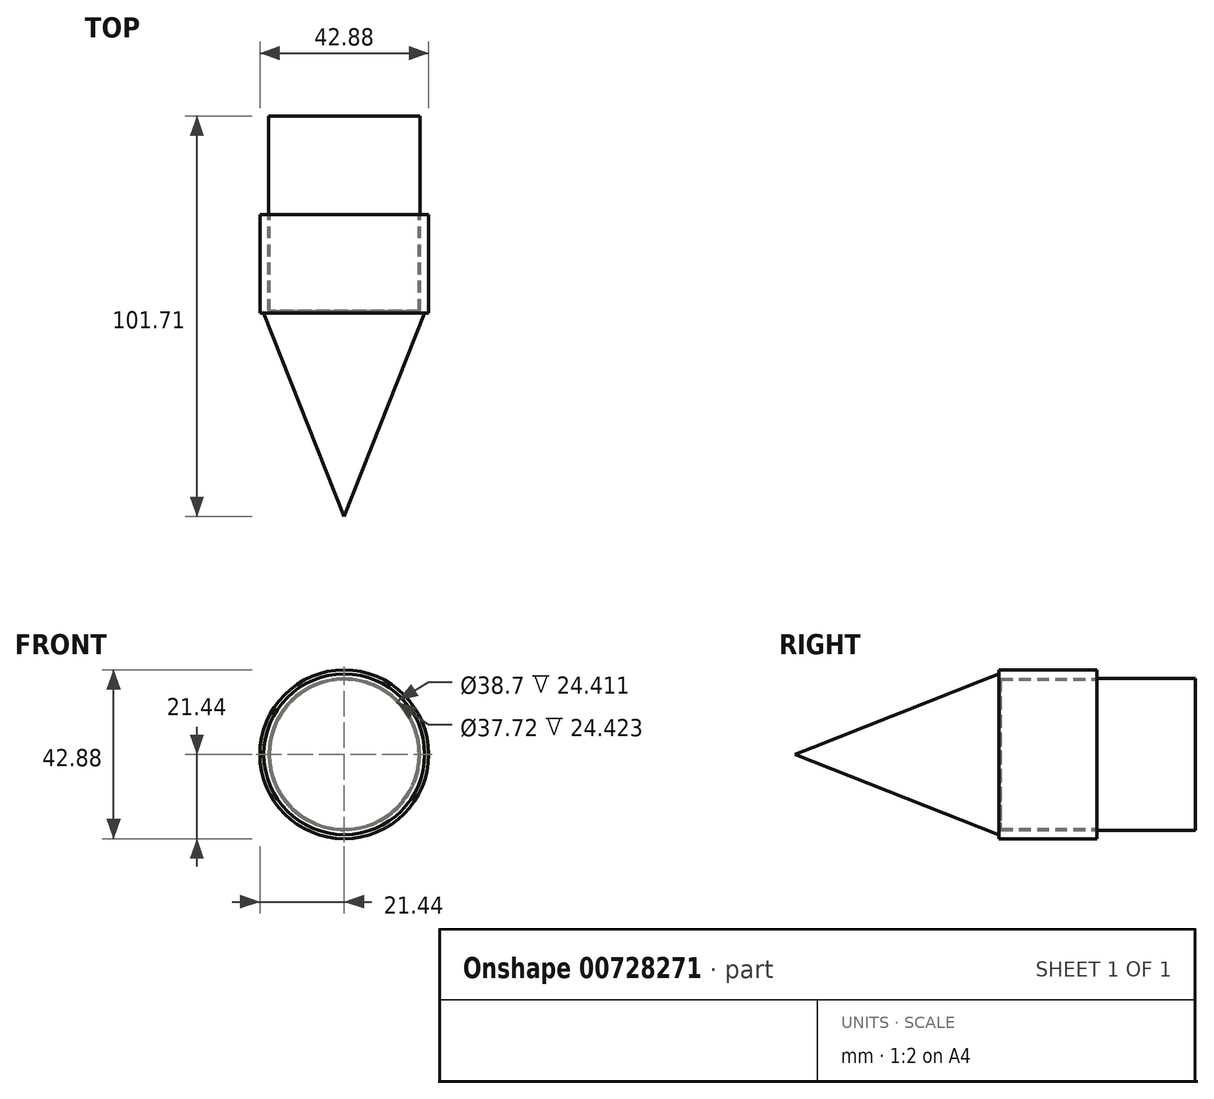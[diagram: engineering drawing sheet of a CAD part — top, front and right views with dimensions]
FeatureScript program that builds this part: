
annotation { "Feature Type Name" : "Feature", "Feature Type Description" : "" }
export const myFeature = defineFeature(function(context is Context, id is Id, definition is map)
    precondition{}
    {
        {
            var Q0;
            Q0=qCreatedBy(makeId("Front.planeOp"),FACE);
            var sketch = newSketch(context, id + "F0", { "sketchPlane" : qUnion([Q0])});
            skCircle(sketch, "E0", {"center": v(0, 0) * mm, "radius": 21.43 * mm});
            skCircle(sketch, "E1", {"center": v(0, 0) * mm, "radius": 19.35 * mm});
            skSolve(sketch);
        }
        {
            var Q0;
            Q0 = qSketchRegion(id + "F0", true);
            extrude(context, id + "F1", {"entities" : qUnion([Q0]), "depth" : 25 * mm, "offsetDistance" : 25 * mm});
        }
        {
            var Q0;
            Q0=qCreatedBy(makeId("Right.planeOp"),FACE);
            var sketch = newSketch(context, id + "F2", { "sketchPlane" : qUnion([Q0])});
            skLineSegment(sketch, "E2", {"start": v(-24.89, 0) * mm, "end": v(-76.7, 0) * mm});
            skLineSegment(sketch, "E3", {"start": v(-76.7, 0) * mm, "end": v(-24.38, 20.67) * mm});
            skLineSegment(sketch, "E4", {"start": v(-24.38, 20.67) * mm, "end": v(-24.89, 0) * mm});
            skLineSegment(sketch, "E5", {"start": v(0, 0) * mm, "end": v(-12.13, 0) * mm});
            skSolve(sketch);
        }
        {
            var Q0;
            Q0 = qSketchRegion(id + "F2", true);
            var Q1;
            Q1=sQuery(id+"F2.wireOp",EDGE,"E5");
            revolve(context, id + "F3", {"operationType" : NewBodyOperationType.ADD, "surfaceOperationType" : NewSurfaceOperationType.NEW, "entities" : qUnion([Q0]), "axis" : qUnion([Q1]), "revolveType" : RevolveType.FULL});
        }
        {
            var Q0;
            Q0=makeQuery(id+"F1.opExtrude","CAP_FACE",FACE,{"disambiguationData":[OSD([sQuery(id+"F0.wireOp",EDGE,"E0"),sQuery(id+"F0.wireOp",EDGE,"E1")])],"isStart":true});
            var sketch = newSketch(context, id + "F4", { "sketchPlane" : qUnion([Q0])});
            skCircle(sketch, "E6", {"center": v(0, 0) * mm, "radius": 19.26 * mm});
            skSolve(sketch);
        }
        {
            var Q0;
            Q0=qCreatedBy(makeId("Front.planeOp"),FACE);
            var sketch = newSketch(context, id + "F5", { "sketchPlane" : qUnion([Q0])});
            skCircle(sketch, "E7", {"center": v(0, 0) * mm, "radius": 19.15 * mm});
            skCircle(sketch, "E8", {"center": v(0, 0) * mm, "radius": 18.86 * mm});
            skSolve(sketch);
        }
        {
            var Q0;
            Q0 = qSketchRegion(id + "F5", true);
            extrude(context, id + "F6", {"entities" : qUnion([Q0]), "operationType" : NewBodyOperationType.ADD, "depth" : 25 * mm, "offsetDistance" : 25 * mm});
        }
        {
            var Q0;
            Q0=makeQuery(id+"F4.imprint","IMPRINT",FACE,{"disambiguationData":[TD([[makeQuery(id+"F4.imprint","IMPRINT",EDGE,{"derivedFrom":sQuery(id+"F4.wireOp",EDGE,"E6")}),1.0]])]});
            extrude(context, id + "F7", {"entities" : qUnion([Q0]), "operationType" : NewBodyOperationType.ADD, "depth" : 25 * mm, "offsetDistance" : 25 * mm});
        }
    });
